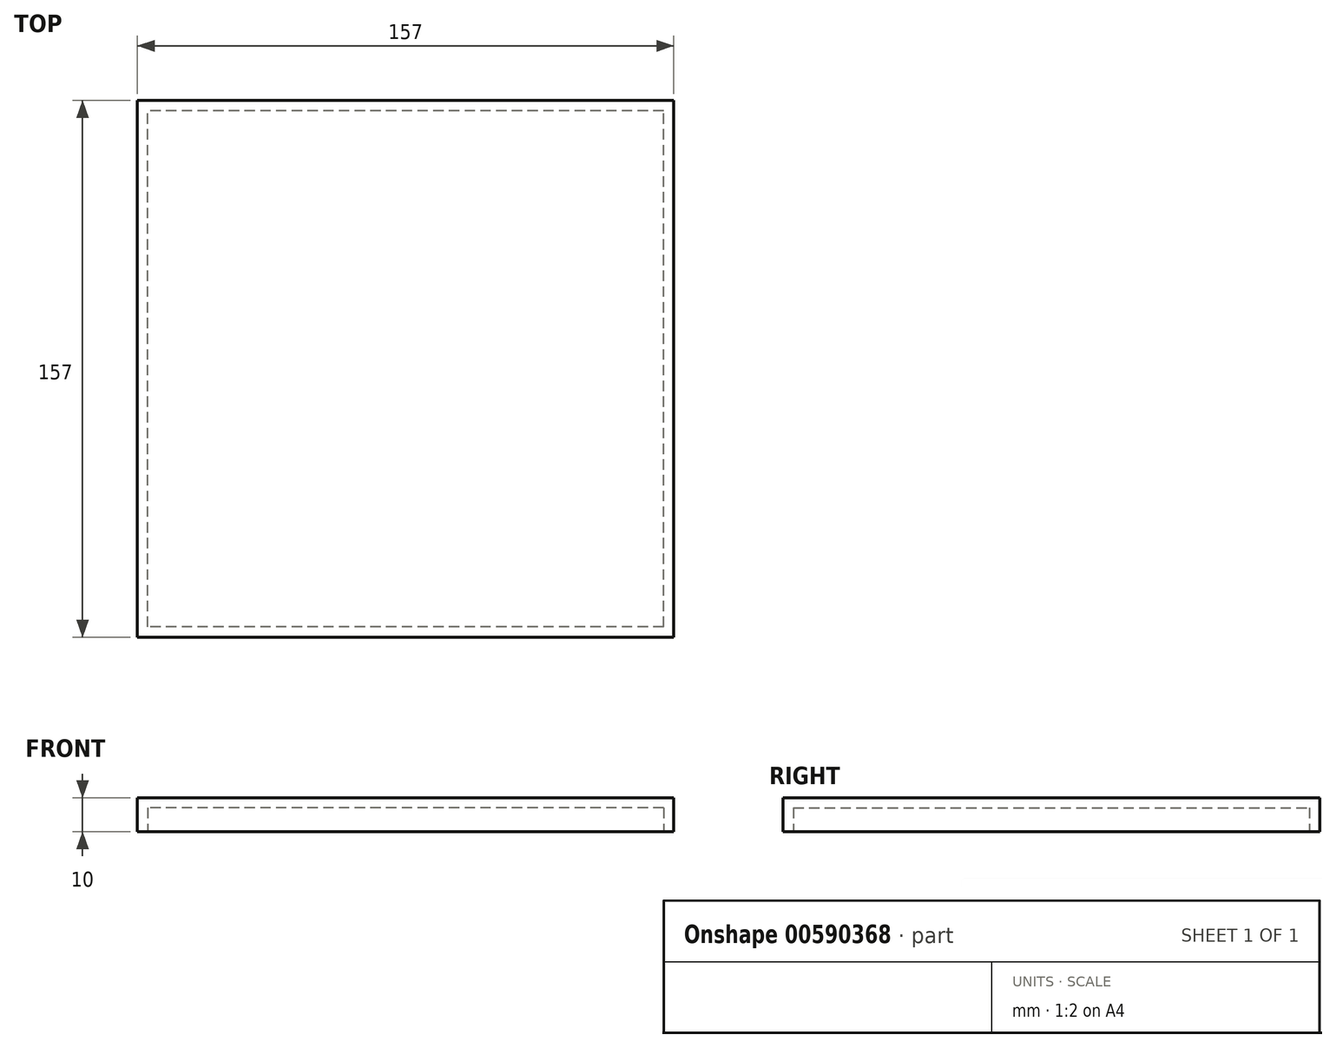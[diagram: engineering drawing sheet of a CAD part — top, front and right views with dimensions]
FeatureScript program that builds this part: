
annotation { "Feature Type Name" : "Feature", "Feature Type Description" : "" }
export const myFeature = defineFeature(function(context is Context, id is Id, definition is map)
    precondition{}
    {
        {
            var Q0;
            Q0=qCreatedBy(makeId("Top.planeOp"),FACE);
            var sketch = newSketch(context, id + "F0", { "sketchPlane" : qUnion([Q0])});
            skLineSegment(sketch, "E0.bottom", {"start": v(78.5, 78.5) * mm, "end": v(-78.5, 78.5) * mm});
            skLineSegment(sketch, "E0.top", {"start": v(78.5, -78.5) * mm, "end": v(-78.5, -78.5) * mm});
            skLineSegment(sketch, "E0.left", {"start": v(78.5, 78.5) * mm, "end": v(78.5, -78.5) * mm});
            skLineSegment(sketch, "E0.right", {"start": v(-78.5, 78.5) * mm, "end": v(-78.5, -78.5) * mm});
            skPoint(sketch, "E0.middle", {"position": v(0, 0) * mm});
            skSolve(sketch);
        }
        {
            var Q0;
            Q0 = qSketchRegion(id + "F0", true);
            extrude(context, id + "F1", {"entities" : qUnion([Q0]), "depth" : 10 * mm, "offsetDistance" : 25 * mm});
        }
        {
            var Q0;
            Q0=qCreatedBy(makeId("Top.planeOp"),FACE);
            var sketch = newSketch(context, id + "F2", { "sketchPlane" : qUnion([Q0])});
            skLineSegment(sketch, "E1.bottom", {"start": v(75.5, -75.5) * mm, "end": v(-75.5, -75.5) * mm});
            skLineSegment(sketch, "E1.top", {"start": v(75.5, 75.5) * mm, "end": v(-75.5, 75.5) * mm});
            skLineSegment(sketch, "E1.left", {"start": v(75.5, -75.5) * mm, "end": v(75.5, 75.5) * mm});
            skLineSegment(sketch, "E1.right", {"start": v(-75.5, -75.5) * mm, "end": v(-75.5, 75.5) * mm});
            skSolve(sketch);
        }
        {
            var Q0;
            Q0 = qSketchRegion(id + "F2", true);
            extrude(context, id + "F3", {"entities" : qUnion([Q0]), "operationType" : NewBodyOperationType.REMOVE, "depth" : 7 * mm, "offsetDistance" : 25 * mm});
        }
    });
